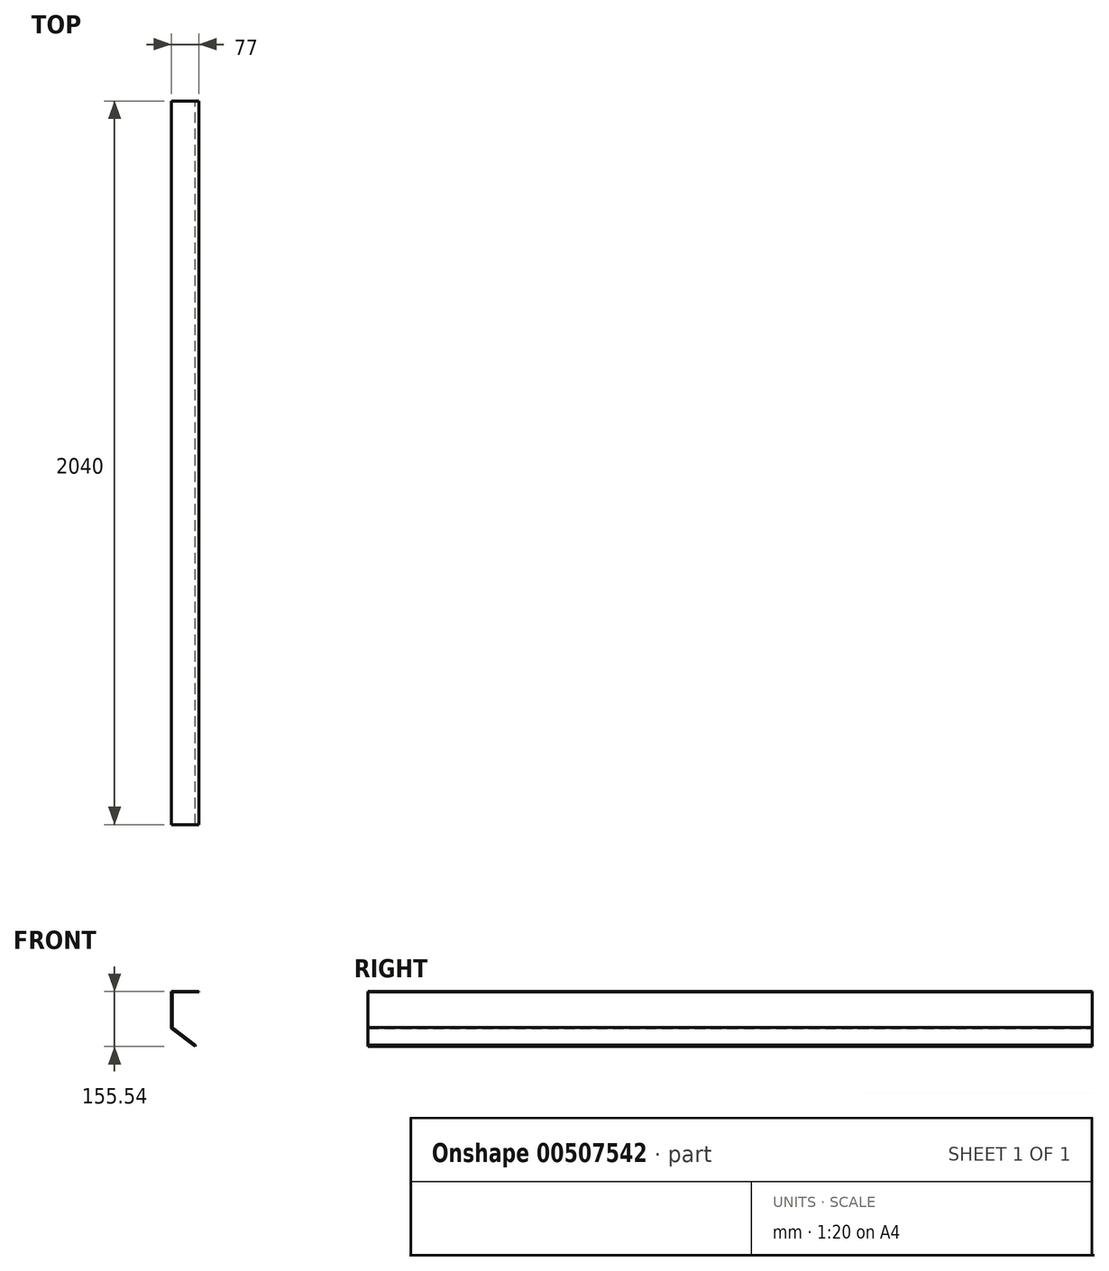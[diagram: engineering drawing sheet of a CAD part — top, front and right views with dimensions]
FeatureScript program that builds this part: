
annotation { "Feature Type Name" : "Feature", "Feature Type Description" : "" }
export const myFeature = defineFeature(function(context is Context, id is Id, definition is map)
    precondition{}
    {
        {
            var Q0;
            Q0=qCreatedBy(makeId("Front.planeOp"),FACE);
            var sketch = newSketch(context, id + "F0", { "sketchPlane" : qUnion([Q0])});
            skLineSegment(sketch, "E0.top", {"start": v(-5, 153.54) * mm, "end": v(70, 153.54) * mm});
            skLineSegment(sketch, "E0.left", {"start": v(-5, 53.54) * mm, "end": v(-5, 153.54) * mm});
            skLineSegment(sketch, "E1", {"start": v(60, 3.67) * mm, "end": v(-5, 53.67) * mm});
            skLineSegment(sketch, "E2", {"start": v(70, 153.54) * mm, "end": v(70, 155.54) * mm});
            skLineSegment(sketch, "E3", {"start": v(70, 155.54) * mm, "end": v(-7, 155.54) * mm});
            skLineSegment(sketch, "E4", {"start": v(-7, 155.54) * mm, "end": v(-7, 51.54) * mm});
            skLineSegment(sketch, "E5", {"start": v(-7, 51.54) * mm, "end": v(60, 0) * mm});
            skLineSegment(sketch, "E6", {"start": v(60, 3.67) * mm, "end": v(60, 0) * mm});
            skSolve(sketch);
        }
        {
            var Q0;
            Q0 = qSketchRegion(id + "F0", true);
            extrude(context, id + "F1", {"entities" : qUnion([Q0]), "depth" : 2040 * mm, "offsetDistance" : 25 * mm});
        }
    });
